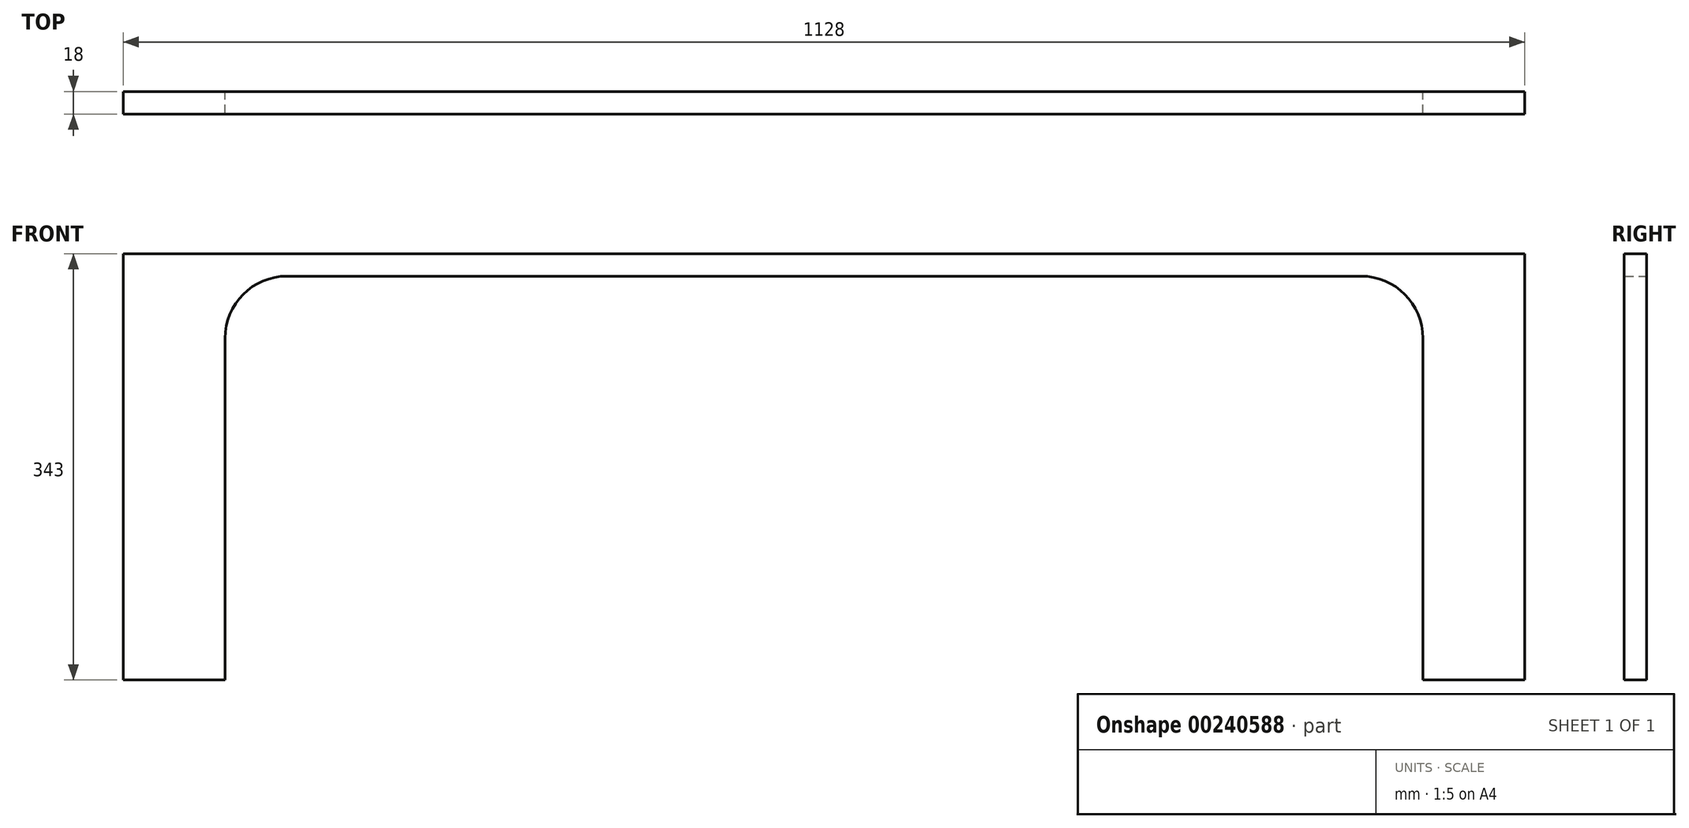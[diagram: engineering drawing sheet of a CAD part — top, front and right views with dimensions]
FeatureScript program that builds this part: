
annotation { "Feature Type Name" : "Feature", "Feature Type Description" : "" }
export const myFeature = defineFeature(function(context is Context, id is Id, definition is map)
    precondition{}
    {
        {
            var Q0;
            Q0=qCreatedBy(makeId("Front.planeOp"),FACE);
            var sketch = newSketch(context, id + "F0", { "sketchPlane" : qUnion([Q0])});
            skLineSegment(sketch, "E0.bottom", {"start": v(0, 0) * mm, "end": v(1128, 0) * mm});
            skLineSegment(sketch, "E0.top", {"start": v(0, 343) * mm, "end": v(1128, 343) * mm});
            skLineSegment(sketch, "E0.left", {"start": v(0, 0) * mm, "end": v(0, 343) * mm});
            skLineSegment(sketch, "E0.right", {"start": v(1128, 0) * mm, "end": v(1128, 343) * mm});
            skLineSegment(sketch, "E1.bottom", {"start": v(82, 0) * mm, "end": v(1046, 0) * mm});
            skLineSegment(sketch, "E1.top", {"start": v(132, 325) * mm, "end": v(996, 325) * mm});
            skLineSegment(sketch, "E1.left", {"start": v(82, 0) * mm, "end": v(82, 275) * mm});
            skLineSegment(sketch, "E1.right", {"start": v(1046, 0) * mm, "end": v(1046, 275) * mm});
            skPoint(sketch, "E2.visualSharp", {"position": v(82, 325) * mm});
            skArc(sketch, "E2.filletArc", {"start": v(132, 325) * mm, "mid": v(96.64, 310.36) * mm, "end": v(82, 275) * mm});
            skPoint(sketch, "E3.visualSharp", {"position": v(1046, 325) * mm});
            skArc(sketch, "E3.filletArc", {"start": v(1046, 275) * mm, "mid": v(1031.36, 310.36) * mm, "end": v(996, 325) * mm});
            skSolve(sketch);
        }
        {
            var Q0;
            Q0=makeQuery(id+"F0.imprint","IMPRINT",FACE,{"disambiguationData":[TD([[makeQuery(id+"F0.imprint","IMPRINT",EDGE,{"derivedFrom":sQuery(id+"F0.wireOp",EDGE,"E1.top")}),1.0]])]});
            extrude(context, id + "F1", {"entities" : qUnion([Q0]), "depth" : 18 * mm});
        }
    });
